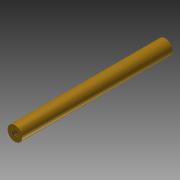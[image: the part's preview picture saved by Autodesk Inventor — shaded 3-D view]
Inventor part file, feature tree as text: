
AUTODESK INVENTOR PART (.ipt)
format: ipt  version: 2014 SP1 (Build 180222100, 222)  size: 81,408 bytes
history: native  units: in
note: dims shown in document units (in); Inventor stores cm internally (conversion verified against a paired STEP export)
features: sketch x3, hole x2, extrude x1
ambient origin geometry x8: Origin, YZ Plane, XZ Plane, XY Plane, X Axis, Y Axis, Z Axis, Center Point
bodies: Solid1 (feature_tree)
feature tree (6):
  extrude  "Extrusion1"  Depth=5.18in TaperAngle=0.0deg
  hole  "Hole1"  [1 undecoded]
  hole  "Hole2"  [1 undecoded]
  sketch  "Sketch1"  dims[d0=0.5in d1=5.18in d2=0.0in]
  sketch  "Sketch2"  dims[d3=0.196in d4=1.0in d5=0.375in d6=0.25in d7=0.5635in d8=1.0in d9=0.8108in]
  sketch  "Sketch3"  dims[d10=0.196in d11=1.0in d12=0.375in d13=0.25in d14=0.5635in d15=1.0in d16=0.8108in]
note: 2 required parameter values undecoded (feature->parameter linkage not recoverable at this tier; creation-order binding heuristic only, values carry confidence <= 0.55)
